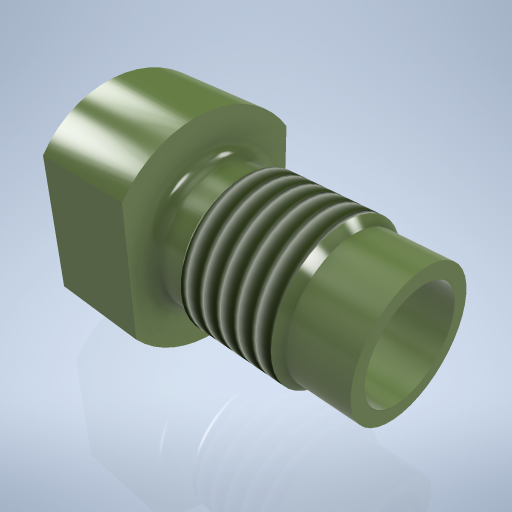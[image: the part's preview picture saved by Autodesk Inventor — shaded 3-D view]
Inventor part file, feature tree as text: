
AUTODESK INVENTOR PART (.ipt)
format: ipt  version: 2024.2 (Build 282272000, 272)  size: 356,352 bytes
history: native  units: mm
features: sketch x3, revolve x1, thread x1, hole x1, extrude x1, fillet x1
ambient origin geometry x8: Origin, YZ Plane, XZ Plane, XY Plane, X Axis, Y Axis, Z Axis, Center Point
bodies: Volumenkörper1 (feature_tree)
feature tree (8):
  revolve  "Umdrehung1"
  thread  "Gewinde1"  [1 undecoded]
  hole  "Bohrung1"  [1 undecoded]
  extrude  "Extrusion1"  Depth=28.0mm
  fillet  "Rundung1"  Radius=28.0mm
  sketch  "Skizze1"  dims[d1=42.0mm d2=20.0mm]
  sketch  "Skizze2"  dims[d3=18.0mm d4=5.0mm d5=28.0mm]
  sketch  "Skizze3"  dims[d6=8.0mm d7=30.0mm d8=90.0deg d9=13.0mm d10=0.0mm d11=14.0mm d12=6.0mm d13=4.0mm d14=2.0mm d15=90.0deg d16=8.0mm d17=0.0mm d18=24.0mm d19=10.0mm d20=0.0mm d21=2.0mm]
note: 2 required parameter values undecoded (feature->parameter linkage not recoverable at this tier; creation-order binding heuristic only, values carry confidence <= 0.55)
